# Revit family: Furniture-Floor_Mount-Vanity-KOHLER-AMERISSIC-K-98982T_1
name_source: partatom
category: Plumbing Fixtures
revit_build: Autodesk Revit 2017 (Build: 20160225_1515(x64)
units: mm (PartAtom-declared; Revit-internal decimal feet)

## family parameters
Cut with Voids When Loaded = No
Host = Face
OmniClass Number = 23.31.25.13
OmniClass Title = Bathroom Cabinets
Part Type = Normal
Room Calculation Point = No
Round Connector Dimension = Use Diameter
Shared = No

## types (1)
- F04-Classical Ginger Yellow
    ADA Compliant = No
    Assembly Code = D2010400
    CW Connection = No
    Cold Water Inlet = Cold Water Inlet
    Date Modified = 03/09/2021
    Default Elevation = 0"
    Description = 940 MM SET W/MEMOIRS LAV 1
    Drain Included = No
    Finish = KOHLER-Wood-F04-Classical_Ginger_Yellow
    HW Connection = No
    Hardware Included = No
    Height = 33 1/16"
    Hot Water Inlet = Hot Water Inlet
    Length = 24 5/8"
    Manufacturer = KOHLER Co.
    Master Format 2014 = 22 41 16
    Master Format 2014 Name = Residential Lavatories and Sinks
    Material = Solid Wood Construction
    Model = K-98982T-F04
    Product Name = AMERISSIC
    Product Page URL = https://www.kohler.com.cn
    Type = 1
    URL = http://www.kohler.com.cn
    Vent Connection = No
    Waste Connection = Yes
    Waste Water Outlet = Waste Water Outlet
    WaterSense Certified = No
    Width = 37"

## geometry (parser evidence)
native form markers: Sweep x6
no freeform markers — native parametric forms only
